# Revit family: PGN
name_source: partatom
category: Lighting Fixtures
units: mm (PartAtom-declared; Revit-internal decimal feet)

## family parameters
Cut with Voids When Loaded = No
Host = Face
Light Source = Yes
OmniClass Number = 23.80.70.11.21
OmniClass Title = Emergency Lighting
Part Type = Normal
Room Calculation Point = No
Round Connector Dimension = Use Diameter
Shared = No

## types (4) — shared parameters
Color Filter = 16777215
Default Elevation = 48"
Description = High Performance LED Sconce
Dimming Lamp Color Temperature Shift = <None>
Emit from Line Length = 5"
Family = Outdoor Emergency Lighting
Lamp = 4 HIGH OUTPUT LED
Light Source Symbol Size = 1/2"
Manufacturer = Dual-lite
Model = PGN
URL = https://www.currentlighting.com
Wattage Comments = 12-17 W

## per-type parameters (varying)
| type | Backbox |
| PGN-Black | Black |
| PGN-White | White |
| PGN-Dark Bronze | Dark Bronze |
| PGN-SAL | Platinum Silver |

## geometry (parser evidence)
native form markers: Blend x2, Sweep x1
no freeform markers — native parametric forms only
